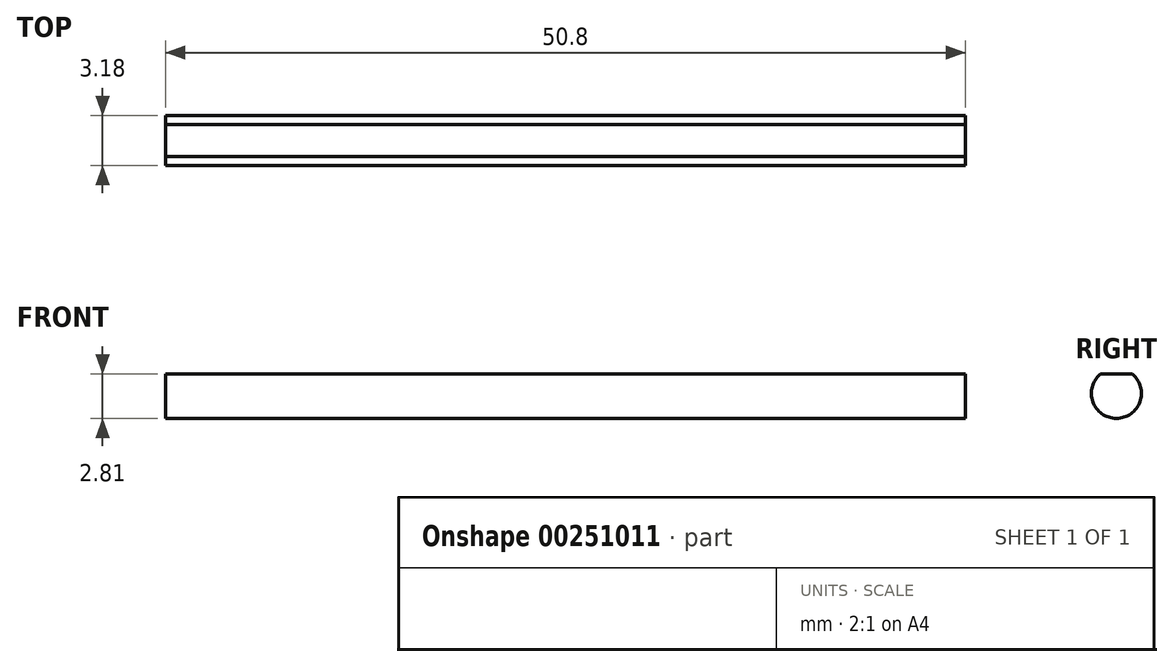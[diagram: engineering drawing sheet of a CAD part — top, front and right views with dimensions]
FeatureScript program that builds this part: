
annotation { "Feature Type Name" : "Feature", "Feature Type Description" : "" }
export const myFeature = defineFeature(function(context is Context, id is Id, definition is map)
    precondition{}
    {
        {
            var Q0;
            Q0=qCreatedBy(makeId("Right.planeOp"),FACE);
            var sketch = newSketch(context, id + "F0", { "sketchPlane" : qUnion([Q0])});
            skArc(sketch, "E0", {"start": v(-1.02, 1.22) * mm, "mid": v(0, -1.59) * mm, "end": v(1.02, 1.22) * mm});
            skLineSegment(sketch, "E1", {"start": v(-1.02, 1.22) * mm, "end": v(1.02, 1.22) * mm});
            skSolve(sketch);
        }
        {
            var Q0;
            Q0=makeQuery(id+"F0.imprint","IMPRINT",FACE,{"disambiguationData":[TD([[makeQuery(id+"F0.imprint","IMPRINT",EDGE,{"derivedFrom":sQuery(id+"F0.wireOp",EDGE,"E0")}),1.0]])]});
            extrude(context, id + "F1", {"entities" : qUnion([Q0]), "depth" : 50.8 * mm});
        }
    });
